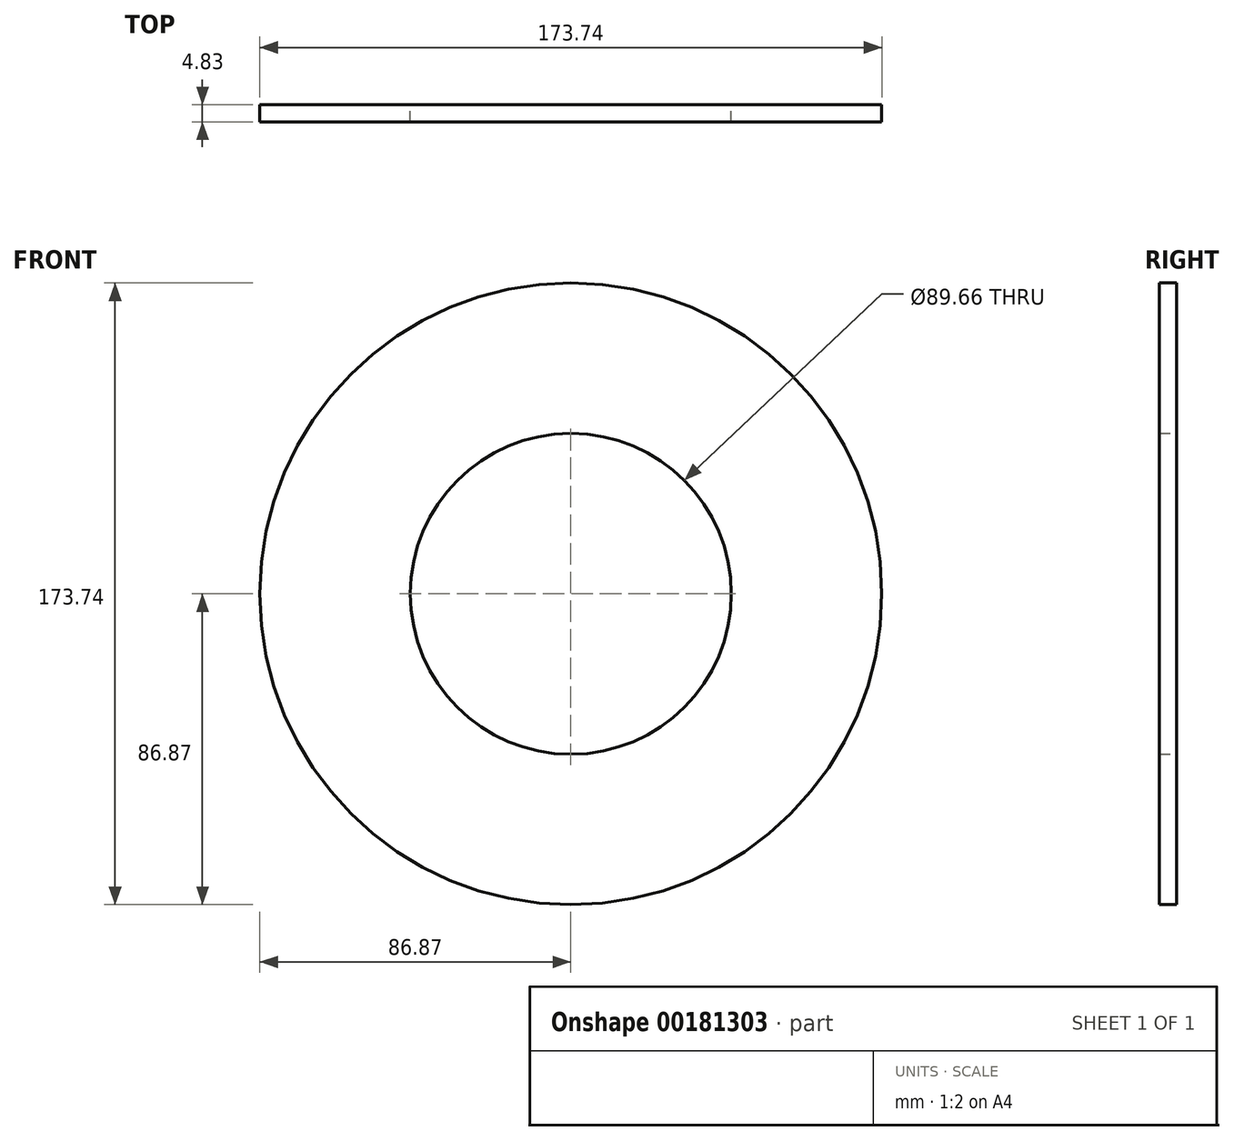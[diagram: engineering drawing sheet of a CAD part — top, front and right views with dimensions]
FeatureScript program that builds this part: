
annotation { "Feature Type Name" : "Feature", "Feature Type Description" : "" }
export const myFeature = defineFeature(function(context is Context, id is Id, definition is map)
    precondition{}
    {
        {
            var Q0;
            Q0=qCreatedBy(makeId("Front.planeOp"),FACE);
            var sketch = newSketch(context, id + "F0", { "sketchPlane" : qUnion([Q0])});
            skCircle(sketch, "E0", {"center": v(0, 0) * mm, "radius": 86.87 * mm});
            skCircle(sketch, "E1", {"center": v(0, 0) * mm, "radius": 44.83 * mm});
            skSolve(sketch);
        }
        {
            var Q0;
            Q0 = qSketchRegion(id + "F0", true);
            extrude(context, id + "F1", {"entities" : qUnion([Q0]), "depth" : 4.83 * mm});
        }
    });
